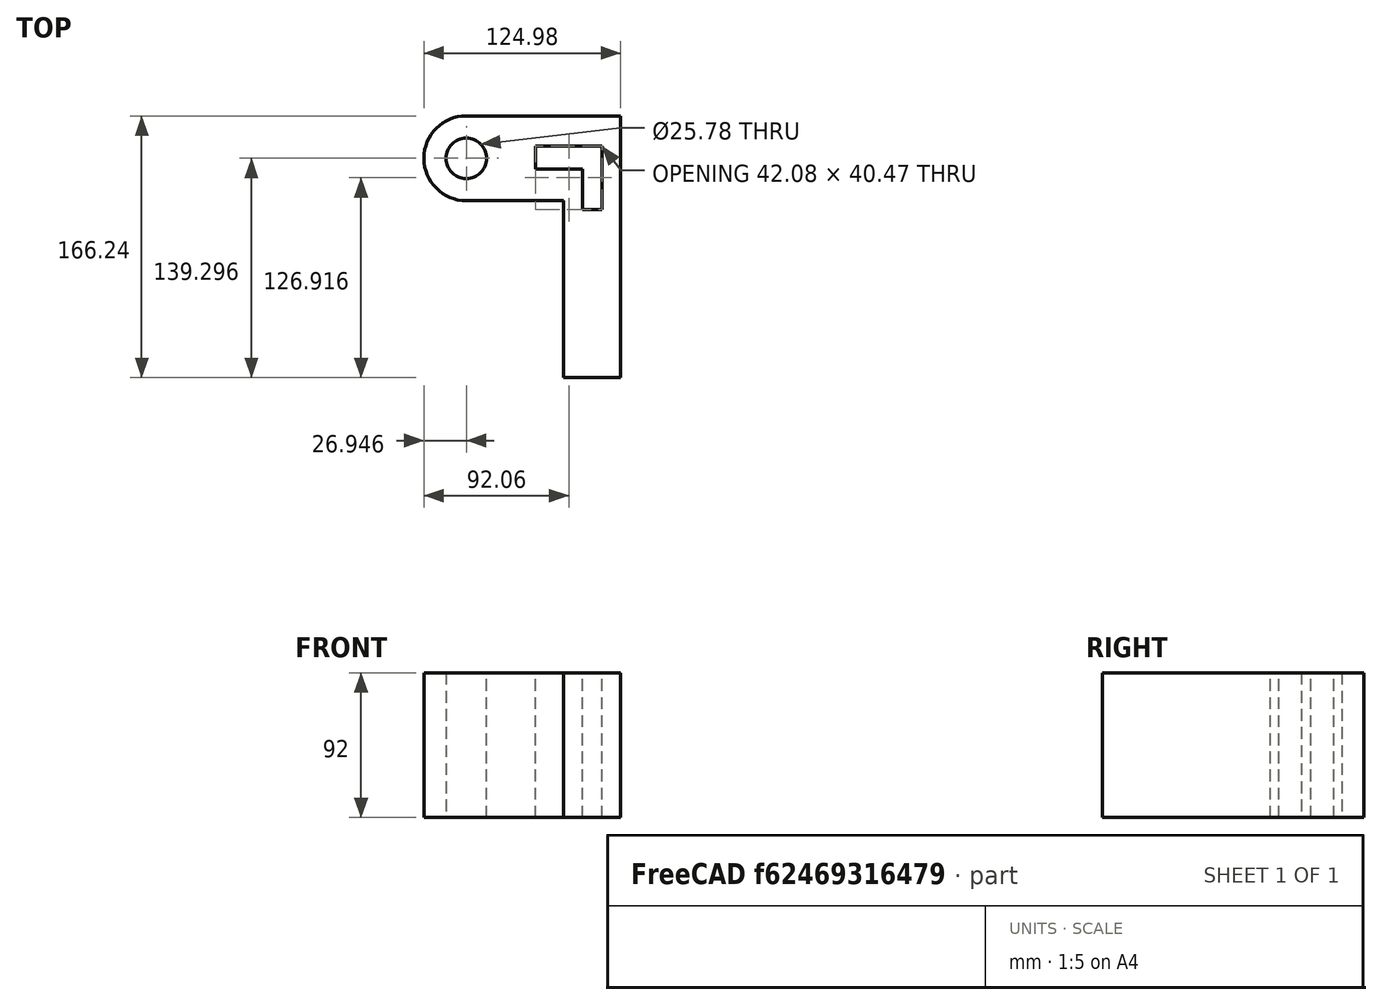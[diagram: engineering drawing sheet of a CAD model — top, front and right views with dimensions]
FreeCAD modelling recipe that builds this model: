
FCSTD DOCUMENT  (FreeCAD 0.19R17171 (Git))
Label: Fem2
License: CC-BY 3.0
LicenseURL: http://creativecommons.org/licenses/by/3.0/
objects: Sketcher::SketchObject×1, PartDesign::Pad×1, Fem::FemMeshShapeNetgenObject×1, Fem::FemAnalysis×1
note: 3 computed .brp shape members not serialized (recipe doc carries the construction recipe); baked Part::Feature solids carry a one-line shape summary decoded from their .brp

FEATURE [Sketcher::SketchObject] Sketch
  MapMode = 5
  sketch-geometry (13):
    g0: ArcOfCircle CenterX=-29.9237 CenterY=19.9863 CenterZ=0 NormalX=0 NormalY=0 NormalZ=1 AngleXU=0 Radius=26.9466 StartAngle=1.5708 EndAngle=4.71239
    g1: LineSegment StartX=-29.9237 StartY=46.933 StartZ=0 EndX=68.1073 EndY=46.933 EndZ=0
    g2: LineSegment StartX=68.1073 StartY=46.933 StartZ=0 EndX=68.1073 EndY=-119.309 EndZ=0
    g3: LineSegment StartX=68.1073 StartY=-119.309 StartZ=0 EndX=31.7141 EndY=-119.309 EndZ=0
    g4: LineSegment StartX=31.7141 StartY=-119.309 StartZ=0 EndX=31.7141 EndY=-6.96029 EndZ=0
    g5: LineSegment StartX=31.7141 StartY=-6.96029 StartZ=0 EndX=-29.9236 EndY=-6.96029 EndZ=0
    g6: Circle CenterX=-29.9237 CenterY=19.9863 CenterZ=0 NormalX=0 NormalY=0 NormalZ=1 AngleXU=0 Radius=12.8881
    g7: LineSegment StartX=14.1478 StartY=27.839 StartZ=0 EndX=56.2317 EndY=27.839 EndZ=0
    g8: LineSegment StartX=56.2317 StartY=27.839 StartZ=0 EndX=56.2317 EndY=-12.6263 EndZ=0
    g9: LineSegment StartX=56.2317 StartY=-12.6263 StartZ=0 EndX=43.9303 EndY=-12.6263 EndZ=0
    g10: LineSegment StartX=43.9303 StartY=-12.6263 StartZ=0 EndX=43.9303 EndY=13.2715 EndZ=0
    g11: LineSegment StartX=43.9303 StartY=13.2715 StartZ=0 EndX=14.1478 EndY=13.2715 EndZ=0
    g12: LineSegment StartX=14.1478 StartY=13.2715 StartZ=0 EndX=14.1478 EndY=27.839 EndZ=0
  constraints (25):
    c: Tangent(g0,g1)
    c: Coincident(g1,g2)
    c: Vertical(g2)
    c: Coincident(g2,g3)
    c: Horizontal(g3)
    c: Coincident(g3,g4)
    c: Vertical(g4)
    c: Coincident(g4,g5)
    c: Coincident(g5,g0)
    c: Horizontal(g5)
    c: Horizontal(g1)
    c: Tangent(g0,g5)
    c: Coincident(g6,g0)
    c: Horizontal(g7)
    c: Coincident(g7,g8)
    c: Vertical(g8)
    c: Coincident(g8,g9)
    c: Horizontal(g9)
    c: Coincident(g9,g10)
    c: Vertical(g10)
    c: Coincident(g10,g11)
    c: Horizontal(g11)
    c: Coincident(g11,g12)
    c: Coincident(g12,g7)
    c: Vertical(g12)
FEATURE [PartDesign::Pad] Pad
  Length = 92
  Length2 = 100
  Profile = -> Sketch
  Type = 0
FEATURE [Fem::FemMeshShapeNetgenObject] Pad_Mesh
  Fineness = 2
  GrowthRate = 0.3
  MaxSize = 1000
  NbSegsPerEdge = 1
  NbSegsPerRadius = 2
  Optimize = true
  SecondOrder = false
  Shape = -> Pad
FEATURE [Fem::FemAnalysis] FemAnalysis
  Group = -> [Pad_Mesh]
